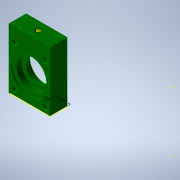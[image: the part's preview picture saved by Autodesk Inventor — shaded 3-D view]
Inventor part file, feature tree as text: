
AUTODESK INVENTOR PART (.ipt)
format: ipt  version: 2020 (Build 240168000, 168)  size: 514,560 bytes
history: native  units: in
note: dims shown in document units (in); Inventor stores cm internally (conversion verified against a paired STEP export)
features: sketch x4, hole x4, extrude x3
ambient origin geometry x8: Origin, YZ Plane, XZ Plane, XY Plane, X Axis, Y Axis, Z Axis, Center Point
bodies: Solid1 (feature_tree)
feature tree (11):
  extrude  "Extrusion1"  Depth=0.4in TaperAngle=0.0deg
  extrude  "Extrusion2"  Depth=0.25in
  sketch  "Sketch3"  dims[d6=0.213in d7=0.75in d8=0.507in d9=0.25in d10=0.5635in d11=0.25in d12=0.0in]
  extrude  "Extrusion3"  Depth=0.25in
  hole  "Hole1"  [1 undecoded]
  hole  "Hole2"  [1 undecoded]
  sketch  "Sketch4"  dims[d13=0.04in d14=0.75in d15=0.507in d16=0.25in d17=0.5635in d18=1.0in d19=0.8108in d20=0.4583in d21=0.29in d22=0.04in d23=0.75in d24=0.507in d25=0.25in d26=0.5635in d27=1.0in d28=0.8108in d29=0.213in d30=0.75in d31=0.507in d32=0.25in d33=0.5635in d34=0.25in d35=0.0in]
  hole  "Hole3"  [1 undecoded]
  hole  "Hole4"  [1 undecoded]
  sketch  "Sketch1"  dims[d0=0.4in d1=0.0in d2=0.4in d3=0.0in]
  sketch  "Sketch2"  dims[d4=0.6in d5=0.0in]
note: 4 required parameter values undecoded (feature->parameter linkage not recoverable at this tier; creation-order binding heuristic only, values carry confidence <= 0.55)
